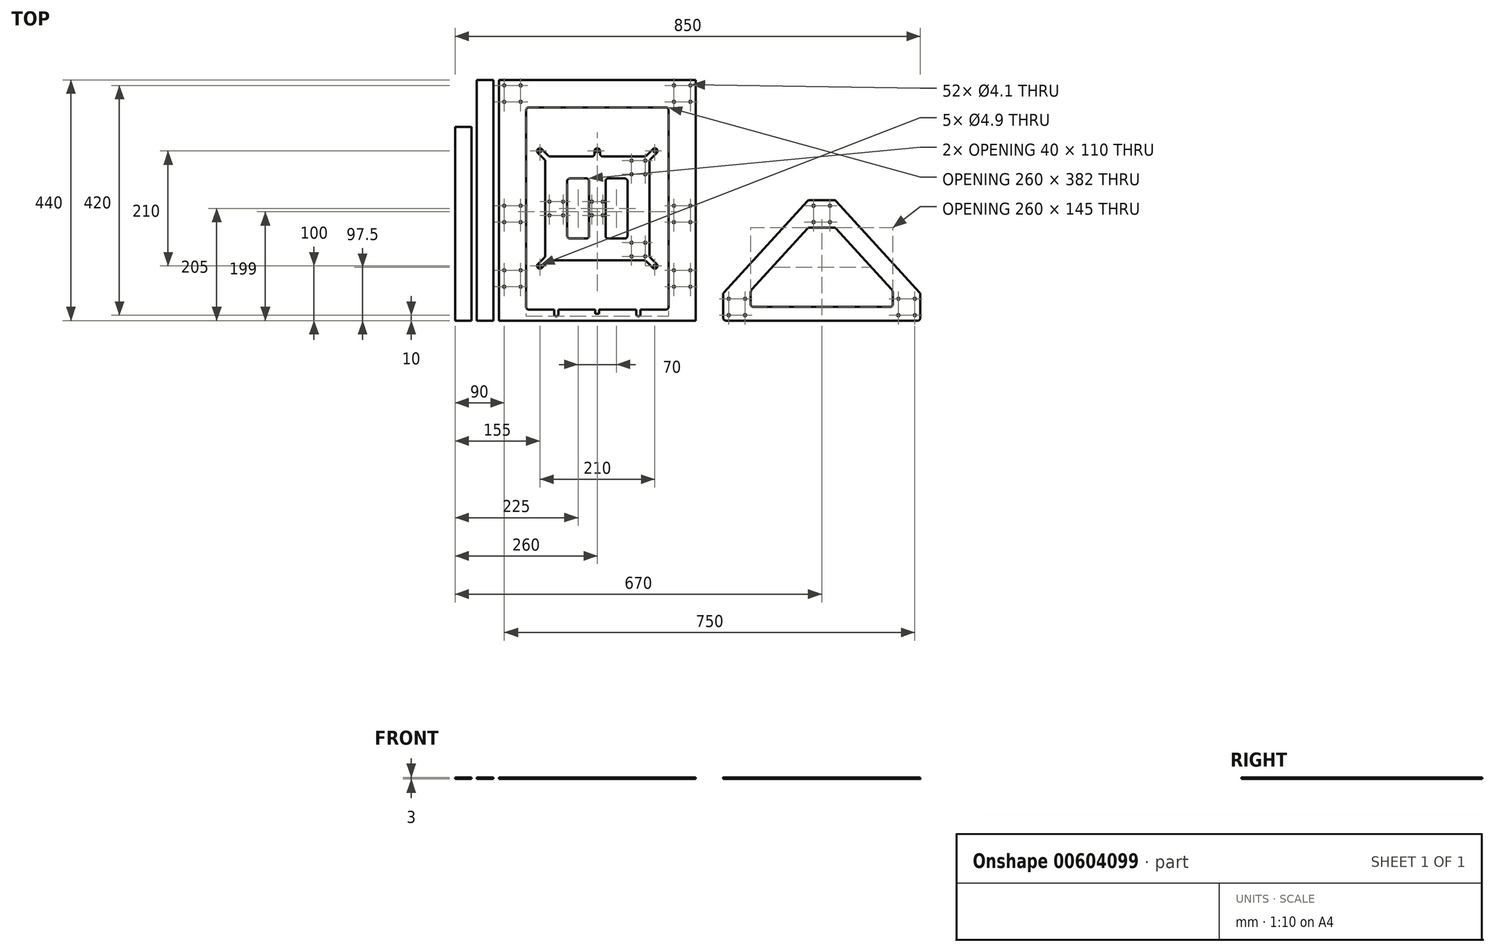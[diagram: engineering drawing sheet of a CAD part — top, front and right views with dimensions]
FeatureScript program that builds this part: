
annotation { "Feature Type Name" : "Feature", "Feature Type Description" : "" }
export const myFeature = defineFeature(function(context is Context, id is Id, definition is map)
    precondition{}
    {
        {
            var Q0;
            Q0=qCreatedBy(makeId("Top.planeOp"),FACE);
            var sketch = newSketch(context, id + "F0", { "sketchPlane" : qUnion([Q0])});
            skLineSegment(sketch, "E0.bottom", {"start": v(0, 0) * mm, "end": v(360, 0) * mm});
            skLineSegment(sketch, "E0.top", {"start": v(0, 440) * mm, "end": v(360, 440) * mm});
            skLineSegment(sketch, "E0.left", {"start": v(0, 0) * mm, "end": v(0, 440) * mm});
            skLineSegment(sketch, "E0.right", {"start": v(360, 0) * mm, "end": v(360, 440) * mm});
            skLineSegment(sketch, "E1.bottom", {"start": v(0, 440) * mm, "end": v(50, 440) * mm, "construction": true});
            skLineSegment(sketch, "E1.top", {"start": v(0, 390) * mm, "end": v(50, 390) * mm, "construction": true});
            skLineSegment(sketch, "E1.left", {"start": v(0, 440) * mm, "end": v(0, 390) * mm, "construction": true});
            skLineSegment(sketch, "E1.right", {"start": v(50, 440) * mm, "end": v(50, 390) * mm, "construction": true});
            skLineSegment(sketch, "E2.bottom", {"start": v(360, 440) * mm, "end": v(310, 440) * mm, "construction": true});
            skLineSegment(sketch, "E2.top", {"start": v(360, 390) * mm, "end": v(310, 390) * mm, "construction": true});
            skLineSegment(sketch, "E2.left", {"start": v(360, 440) * mm, "end": v(360, 390) * mm, "construction": true});
            skLineSegment(sketch, "E2.right", {"start": v(310, 440) * mm, "end": v(310, 390) * mm, "construction": true});
            skLineSegment(sketch, "E3", {"start": v(180, 0) * mm, "end": v(180, 20) * mm, "construction": true});
            skLineSegment(sketch, "E4.bottom", {"start": v(305, 390) * mm, "end": v(55, 390) * mm});
            skLineSegment(sketch, "E4.top", {"start": v(305, 20) * mm, "end": v(259, 20) * mm});
            skLineSegment(sketch, "E4.left", {"start": v(310, 385) * mm, "end": v(310, 25) * mm});
            skLineSegment(sketch, "E4.right", {"start": v(50, 385) * mm, "end": v(50, 25) * mm});
            skLineSegment(sketch, "E5.top", {"start": v(176.5, 12.5) * mm, "end": v(183.5, 12.5) * mm});
            skLineSegment(sketch, "E5.left", {"start": v(176.5, 20) * mm, "end": v(176.5, 12.5) * mm});
            skLineSegment(sketch, "E5.right", {"start": v(183.5, 20) * mm, "end": v(183.5, 12.5) * mm});
            skArc(sketch, "E6", {"start": v(101, 12) * mm, "mid": v(105, 8) * mm, "end": v(109, 12) * mm});
            skLineSegment(sketch, "E7", {"start": v(0, 12) * mm, "end": v(360, 12) * mm, "construction": true});
            skArc(sketch, "E8", {"start": v(251, 12) * mm, "mid": v(255, 8) * mm, "end": v(259, 12) * mm});
            skLineSegment(sketch, "E9.trimOffspring", {"start": v(176.5, 20) * mm, "end": v(109, 20) * mm});
            skCircle(sketch, "E10", {"center": v(10, 62) * mm, "radius": 2.05 * mm});
            skCircle(sketch, "E11.0.1.0", {"center": v(10, 92) * mm, "radius": 2.05 * mm});
            skCircle(sketch, "E11.1.0.0", {"center": v(40, 62) * mm, "radius": 2.05 * mm});
            skCircle(sketch, "E11.1.1.0", {"center": v(40, 92) * mm, "radius": 2.05 * mm});
            skLineSegment(sketch, "E11.direction1", {"start": v(10, 62) * mm, "end": v(40, 62) * mm, "construction": true});
            skLineSegment(sketch, "E11.direction2", {"start": v(10, 62) * mm, "end": v(10, 92) * mm, "construction": true});
            skCircle(sketch, "E12", {"center": v(320, 62) * mm, "radius": 2.05 * mm});
            skCircle(sketch, "E13.0.1.0", {"center": v(320, 92) * mm, "radius": 2.05 * mm});
            skCircle(sketch, "E13.1.0.0", {"center": v(350, 62) * mm, "radius": 2.05 * mm});
            skCircle(sketch, "E13.1.1.0", {"center": v(350, 92) * mm, "radius": 2.05 * mm});
            skLineSegment(sketch, "E13.direction1", {"start": v(320, 62) * mm, "end": v(350, 62) * mm, "construction": true});
            skLineSegment(sketch, "E13.direction2", {"start": v(320, 62) * mm, "end": v(320, 92) * mm, "construction": true});
            skCircle(sketch, "E14", {"center": v(10, 400) * mm, "radius": 2.05 * mm});
            skCircle(sketch, "E15.0.1.0", {"center": v(10, 430) * mm, "radius": 2.05 * mm});
            skCircle(sketch, "E15.1.0.0", {"center": v(40, 400) * mm, "radius": 2.05 * mm});
            skCircle(sketch, "E15.1.1.0", {"center": v(40, 430) * mm, "radius": 2.05 * mm});
            skLineSegment(sketch, "E15.direction1", {"start": v(10, 400) * mm, "end": v(40, 400) * mm, "construction": true});
            skLineSegment(sketch, "E15.direction2", {"start": v(10, 400) * mm, "end": v(10, 430) * mm, "construction": true});
            skCircle(sketch, "E16", {"center": v(320, 400) * mm, "radius": 2.05 * mm});
            skCircle(sketch, "E17.0.1.0", {"center": v(320, 430) * mm, "radius": 2.05 * mm});
            skCircle(sketch, "E17.1.0.0", {"center": v(350, 400) * mm, "radius": 2.05 * mm});
            skCircle(sketch, "E17.1.1.0", {"center": v(350, 430) * mm, "radius": 2.05 * mm});
            skLineSegment(sketch, "E17.direction1", {"start": v(320, 400) * mm, "end": v(350, 400) * mm, "construction": true});
            skLineSegment(sketch, "E17.direction2", {"start": v(320, 400) * mm, "end": v(320, 430) * mm, "construction": true});
            skLineSegment(sketch, "E18", {"start": v(101, 12) * mm, "end": v(101, 20) * mm});
            skLineSegment(sketch, "E19", {"start": v(109, 12) * mm, "end": v(109, 20) * mm});
            skLineSegment(sketch, "E20.trimOffspring", {"start": v(101, 20) * mm, "end": v(55, 20) * mm});
            skLineSegment(sketch, "E21", {"start": v(259, 12) * mm, "end": v(259, 20) * mm});
            skLineSegment(sketch, "E22", {"start": v(251, 12) * mm, "end": v(251, 20) * mm});
            skLineSegment(sketch, "E23.trimOffspring", {"start": v(251, 20) * mm, "end": v(183.5, 20) * mm});
            skLineSegment(sketch, "E24.bottom", {"start": v(350, 92) * mm, "end": v(320, 92) * mm, "construction": true});
            skLineSegment(sketch, "E24.top", {"start": v(350, 62) * mm, "end": v(320, 62) * mm, "construction": true});
            skLineSegment(sketch, "E24.left", {"start": v(350, 92) * mm, "end": v(350, 62) * mm, "construction": true});
            skLineSegment(sketch, "E24.right", {"start": v(320, 92) * mm, "end": v(320, 62) * mm, "construction": true});
            skPoint(sketch, "E24.middle", {"position": v(335, 77) * mm});
            skLineSegment(sketch, "E25", {"start": v(310, 20) * mm, "end": v(360, 20) * mm, "construction": true});
            skLineSegment(sketch, "E26", {"start": v(335, 20) * mm, "end": v(335, 77) * mm, "construction": true});
            skLineSegment(sketch, "E27.bottom", {"start": v(10, 92) * mm, "end": v(40, 92) * mm, "construction": true});
            skLineSegment(sketch, "E27.left", {"start": v(10, 92) * mm, "end": v(10, 62) * mm, "construction": true});
            skLineSegment(sketch, "E27.right", {"start": v(40, 92) * mm, "end": v(40, 62) * mm, "construction": true});
            skPoint(sketch, "E27.middle", {"position": v(25, 77) * mm});
            skLineSegment(sketch, "E28", {"start": v(50, 20) * mm, "end": v(0, 20) * mm, "construction": true});
            skLineSegment(sketch, "E29", {"start": v(25, 20) * mm, "end": v(25, 77) * mm, "construction": true});
            skLineSegment(sketch, "E30.bottom", {"start": v(10, 430) * mm, "end": v(40, 430) * mm, "construction": true});
            skLineSegment(sketch, "E30.left", {"start": v(10, 430) * mm, "end": v(10, 400) * mm, "construction": true});
            skLineSegment(sketch, "E30.right", {"start": v(40, 430) * mm, "end": v(40, 400) * mm, "construction": true});
            skPoint(sketch, "E30.middle", {"position": v(25, 415) * mm});
            skLineSegment(sketch, "E31", {"start": v(25, 390) * mm, "end": v(25, 415) * mm, "construction": true});
            skLineSegment(sketch, "E32", {"start": v(25, 415) * mm, "end": v(50, 415) * mm, "construction": true});
            skLineSegment(sketch, "E33.bottom", {"start": v(350, 430) * mm, "end": v(320, 430) * mm, "construction": true});
            skLineSegment(sketch, "E33.top", {"start": v(350, 400) * mm, "end": v(320, 400) * mm, "construction": true});
            skLineSegment(sketch, "E33.left", {"start": v(350, 430) * mm, "end": v(350, 400) * mm, "construction": true});
            skLineSegment(sketch, "E33.right", {"start": v(320, 430) * mm, "end": v(320, 400) * mm, "construction": true});
            skPoint(sketch, "E33.middle", {"position": v(335, 415) * mm});
            skLineSegment(sketch, "E34", {"start": v(335, 415) * mm, "end": v(335, 390) * mm, "construction": true});
            skLineSegment(sketch, "E35", {"start": v(335, 415) * mm, "end": v(310, 415) * mm, "construction": true});
            skLineSegment(sketch, "E36", {"start": v(0, 220) * mm, "end": v(50, 220) * mm, "construction": true});
            skLineSegment(sketch, "E37", {"start": v(360, 220) * mm, "end": v(310, 220) * mm, "construction": true});
            skLineSegment(sketch, "E38", {"start": v(25, 220) * mm, "end": v(25, 210) * mm, "construction": true});
            skLineSegment(sketch, "E39", {"start": v(335, 220) * mm, "end": v(335, 210) * mm, "construction": true});
            skLineSegment(sketch, "E40.bottom", {"start": v(10, 210) * mm, "end": v(40, 210) * mm, "construction": true});
            skLineSegment(sketch, "E40.top", {"start": v(10, 180) * mm, "end": v(40, 180) * mm, "construction": true});
            skLineSegment(sketch, "E40.left", {"start": v(10, 210) * mm, "end": v(10, 180) * mm, "construction": true});
            skLineSegment(sketch, "E40.right", {"start": v(40, 210) * mm, "end": v(40, 180) * mm, "construction": true});
            skPoint(sketch, "E40.middle", {"position": v(25, 195) * mm});
            skCircle(sketch, "E41", {"center": v(10, 180) * mm, "radius": 2.05 * mm});
            skCircle(sketch, "E42.0.1.0", {"center": v(10, 210) * mm, "radius": 2.05 * mm});
            skCircle(sketch, "E42.1.0.0", {"center": v(40, 180) * mm, "radius": 2.05 * mm});
            skCircle(sketch, "E42.1.1.0", {"center": v(40, 210) * mm, "radius": 2.05 * mm});
            skLineSegment(sketch, "E42.direction2", {"start": v(10, 180) * mm, "end": v(10, 210) * mm, "construction": true});
            skLineSegment(sketch, "E43.bottom", {"start": v(320, 210) * mm, "end": v(350, 210) * mm, "construction": true});
            skLineSegment(sketch, "E43.top", {"start": v(320, 180) * mm, "end": v(350, 180) * mm, "construction": true});
            skLineSegment(sketch, "E43.left", {"start": v(320, 210) * mm, "end": v(320, 180) * mm, "construction": true});
            skLineSegment(sketch, "E43.right", {"start": v(350, 210) * mm, "end": v(350, 180) * mm, "construction": true});
            skPoint(sketch, "E43.middle", {"position": v(335, 195) * mm});
            skCircle(sketch, "E44", {"center": v(320, 180) * mm, "radius": 2.05 * mm});
            skCircle(sketch, "E45.0.1.0", {"center": v(320, 210) * mm, "radius": 2.05 * mm});
            skCircle(sketch, "E45.1.0.0", {"center": v(350, 180) * mm, "radius": 2.05 * mm});
            skCircle(sketch, "E45.1.1.0", {"center": v(350, 210) * mm, "radius": 2.05 * mm});
            skLineSegment(sketch, "E45.direction2", {"start": v(320, 180) * mm, "end": v(320, 210) * mm, "construction": true});
            skPoint(sketch, "E46.visualSharp", {"position": v(0, 0) * mm});
            skPoint(sketch, "E47.visualSharp", {"position": v(50, 20) * mm});
            skArc(sketch, "E47.filletArc", {"start": v(50, 25) * mm, "mid": v(51.46, 21.46) * mm, "end": v(55, 20) * mm});
            skPoint(sketch, "E48.visualSharp", {"position": v(360, 0) * mm});
            skPoint(sketch, "E49.visualSharp", {"position": v(310, 20) * mm});
            skArc(sketch, "E49.filletArc", {"start": v(305, 20) * mm, "mid": v(308.54, 21.46) * mm, "end": v(310, 25) * mm});
            skPoint(sketch, "E50.visualSharp", {"position": v(360, 440) * mm});
            skPoint(sketch, "E51.visualSharp", {"position": v(310, 390) * mm});
            skArc(sketch, "E51.filletArc", {"start": v(310, 385) * mm, "mid": v(308.54, 388.54) * mm, "end": v(305, 390) * mm});
            skPoint(sketch, "E52.visualSharp", {"position": v(50, 390) * mm});
            skArc(sketch, "E52.filletArc", {"start": v(55, 390) * mm, "mid": v(51.46, 388.54) * mm, "end": v(50, 385) * mm});
            skPoint(sketch, "E53.visualSharp", {"position": v(0, 440) * mm});
            skSolve(sketch);
        }
        {
            var Q0;
            Q0=makeQuery(id+"F0.imprint","IMPRINT",FACE,{"disambiguationData":[TD([[makeQuery(id+"F0.imprint","IMPRINT",EDGE,{"derivedFrom":sQuery(id+"F0.wireOp",EDGE,"E0.bottom")}),1.0]])]});
            extrude(context, id + "F1", {"entities" : qUnion([Q0]), "depth" : 3 * mm, "offsetDistance" : 25 * mm});
        }
        {
            var Q0;
            Q0=qCreatedBy(makeId("Top.planeOp"),FACE);
            var sketch = newSketch(context, id + "F2", { "sketchPlane" : qUnion([Q0])});
            skLineSegment(sketch, "E54", {"start": v(310, 205) * mm, "end": v(50, 205) * mm, "construction": true});
            skLineSegment(sketch, "E55", {"start": v(180, 20) * mm, "end": v(180, 390) * mm, "construction": true});
            skLineSegment(sketch, "E56.bottom", {"start": v(255, 280) * mm, "end": v(105, 280) * mm, "construction": true});
            skLineSegment(sketch, "E56.top", {"start": v(255, 130) * mm, "end": v(105, 130) * mm, "construction": true});
            skLineSegment(sketch, "E56.left", {"start": v(255, 280) * mm, "end": v(255, 130) * mm, "construction": true});
            skLineSegment(sketch, "E56.right", {"start": v(105, 280) * mm, "end": v(105, 130) * mm, "construction": true});
            skCircle(sketch, "E57", {"center": v(180, 310) * mm, "radius": 2.45 * mm});
            skLineSegment(sketch, "E58.1", {"start": v(275, 290.86) * mm, "end": v(275, 119.14) * mm});
            skLineSegment(sketch, "E58.2", {"start": v(265.86, 110) * mm, "end": v(180, 110) * mm});
            skLineSegment(sketch, "E58.3", {"start": v(85, 290.86) * mm, "end": v(85, 119.14) * mm});
            skLineSegment(sketch, "E59", {"start": v(75, 310) * mm, "end": v(105, 280) * mm, "construction": true});
            skArc(sketch, "E60.0.startCap", {"start": v(71.46, 306.46) * mm, "mid": v(71.46, 313.54) * mm, "end": v(78.54, 313.54) * mm});
            skLineSegment(sketch, "E60.0.left", {"start": v(78.54, 313.54) * mm, "end": v(90.6, 301.46) * mm});
            skLineSegment(sketch, "E60.0.right", {"start": v(71.46, 306.46) * mm, "end": v(83.54, 294.4) * mm});
            skPoint(sketch, "E61", {"position": v(282.5, 205) * mm});
            skCircle(sketch, "E62", {"center": v(75, 310) * mm, "radius": 2.45 * mm});
            skArc(sketch, "E63.1.0", {"start": v(78.54, 96.46) * mm, "mid": v(71.46, 96.46) * mm, "end": v(71.46, 103.54) * mm});
            skCircle(sketch, "E63.1.1", {"center": v(75, 100) * mm, "radius": 2.45 * mm});
            skLineSegment(sketch, "E63.1.2", {"start": v(78.54, 96.46) * mm, "end": v(90.6, 108.54) * mm});
            skLineSegment(sketch, "E63.1.3", {"start": v(71.46, 103.54) * mm, "end": v(83.54, 115.6) * mm});
            skLineSegment(sketch, "E63.1.4", {"start": v(75, 100) * mm, "end": v(105, 130) * mm, "construction": true});
            skArc(sketch, "E63.2.0", {"start": v(288.54, 103.54) * mm, "mid": v(288.54, 96.46) * mm, "end": v(281.46, 96.46) * mm});
            skCircle(sketch, "E63.2.1", {"center": v(285, 100) * mm, "radius": 2.45 * mm});
            skLineSegment(sketch, "E63.2.2", {"start": v(288.54, 103.54) * mm, "end": v(276.46, 115.6) * mm});
            skLineSegment(sketch, "E63.2.3", {"start": v(281.46, 96.46) * mm, "end": v(269.4, 108.54) * mm});
            skLineSegment(sketch, "E63.2.4", {"start": v(285, 100) * mm, "end": v(255, 130) * mm, "construction": true});
            skArc(sketch, "E63.3.0", {"start": v(281.46, 313.54) * mm, "mid": v(288.54, 313.54) * mm, "end": v(288.54, 306.46) * mm});
            skCircle(sketch, "E63.3.1", {"center": v(285, 310) * mm, "radius": 2.45 * mm});
            skLineSegment(sketch, "E63.3.2", {"start": v(281.46, 313.54) * mm, "end": v(269.4, 301.46) * mm});
            skLineSegment(sketch, "E63.3.3", {"start": v(288.54, 306.46) * mm, "end": v(276.46, 294.4) * mm});
            skLineSegment(sketch, "E63.3.4", {"start": v(285, 310) * mm, "end": v(255, 280) * mm, "construction": true});
            skLineSegment(sketch, "E64", {"start": v(180, 310) * mm, "end": v(180, 280) * mm, "construction": true});
            skArc(sketch, "E65.0.startCap", {"start": v(175, 310) * mm, "mid": v(180, 315) * mm, "end": v(185, 310) * mm});
            skLineSegment(sketch, "E65.0.left", {"start": v(185, 310) * mm, "end": v(185, 305) * mm});
            skLineSegment(sketch, "E65.0.right", {"start": v(175, 310) * mm, "end": v(175, 305) * mm});
            skLineSegment(sketch, "E66.trimOffspring", {"start": v(170, 300) * mm, "end": v(94.14, 300) * mm});
            skLineSegment(sketch, "E67", {"start": v(265.86, 300) * mm, "end": v(190, 300) * mm});
            skLineSegment(sketch, "E68", {"start": v(94.14, 110) * mm, "end": v(180, 110) * mm});
            skLineSegment(sketch, "E69", {"start": v(75, 310) * mm, "end": v(180, 310) * mm, "construction": true});
            skLineSegment(sketch, "E70.bottom", {"start": v(92.5, 217.5) * mm, "end": v(117.5, 217.5) * mm, "construction": true});
            skLineSegment(sketch, "E70.top", {"start": v(92.5, 192.5) * mm, "end": v(117.5, 192.5) * mm, "construction": true});
            skLineSegment(sketch, "E70.left", {"start": v(92.5, 217.5) * mm, "end": v(92.5, 192.5) * mm, "construction": true});
            skLineSegment(sketch, "E70.right", {"start": v(117.5, 217.5) * mm, "end": v(117.5, 192.5) * mm, "construction": true});
            skPoint(sketch, "E70.middle", {"position": v(105, 205) * mm});
            skCircle(sketch, "E71", {"center": v(92.5, 217.5) * mm, "radius": 2.05 * mm});
            skCircle(sketch, "E72", {"center": v(117.5, 217.5) * mm, "radius": 2.05 * mm});
            skCircle(sketch, "E73", {"center": v(117.5, 192.5) * mm, "radius": 2.05 * mm});
            skCircle(sketch, "E74", {"center": v(92.5, 192.5) * mm, "radius": 2.05 * mm});
            skLineSegment(sketch, "E75.bottom", {"start": v(242.5, 292.5) * mm, "end": v(267.5, 292.5) * mm, "construction": true});
            skLineSegment(sketch, "E75.top", {"start": v(242.5, 267.5) * mm, "end": v(267.5, 267.5) * mm, "construction": true});
            skLineSegment(sketch, "E75.left", {"start": v(242.5, 292.5) * mm, "end": v(242.5, 267.5) * mm, "construction": true});
            skLineSegment(sketch, "E75.right", {"start": v(267.5, 292.5) * mm, "end": v(267.5, 267.5) * mm, "construction": true});
            skPoint(sketch, "E75.middle", {"position": v(255, 280) * mm});
            skCircle(sketch, "E76", {"center": v(242.5, 292.5) * mm, "radius": 2.05 * mm});
            skCircle(sketch, "E77", {"center": v(267.5, 292.5) * mm, "radius": 2.05 * mm});
            skCircle(sketch, "E78", {"center": v(267.5, 267.5) * mm, "radius": 2.05 * mm});
            skCircle(sketch, "E79", {"center": v(242.5, 267.5) * mm, "radius": 2.05 * mm});
            skLineSegment(sketch, "E80.bottom", {"start": v(242.5, 142.5) * mm, "end": v(267.5, 142.5) * mm, "construction": true});
            skLineSegment(sketch, "E80.top", {"start": v(242.5, 117.5) * mm, "end": v(267.5, 117.5) * mm, "construction": true});
            skLineSegment(sketch, "E80.left", {"start": v(242.5, 142.5) * mm, "end": v(242.5, 117.5) * mm, "construction": true});
            skLineSegment(sketch, "E80.right", {"start": v(267.5, 142.5) * mm, "end": v(267.5, 117.5) * mm, "construction": true});
            skPoint(sketch, "E80.middle", {"position": v(255, 130) * mm});
            skCircle(sketch, "E81", {"center": v(242.5, 142.5) * mm, "radius": 2.05 * mm});
            skCircle(sketch, "E82", {"center": v(267.5, 142.5) * mm, "radius": 2.05 * mm});
            skCircle(sketch, "E83", {"center": v(267.5, 117.5) * mm, "radius": 2.05 * mm});
            skCircle(sketch, "E84", {"center": v(242.5, 117.5) * mm, "radius": 2.05 * mm});
            skLineSegment(sketch, "E85.bottom", {"start": v(130, 260) * mm, "end": v(160, 260) * mm});
            skLineSegment(sketch, "E85.top", {"start": v(130, 150) * mm, "end": v(160, 150) * mm});
            skLineSegment(sketch, "E85.left", {"start": v(125, 255) * mm, "end": v(125, 155) * mm});
            skLineSegment(sketch, "E85.right", {"start": v(165, 255) * mm, "end": v(165, 155) * mm});
            skPoint(sketch, "E85.middle", {"position": v(145, 205) * mm});
            skLineSegment(sketch, "E86.bottom", {"start": v(200, 260) * mm, "end": v(230, 260) * mm});
            skLineSegment(sketch, "E86.top", {"start": v(200, 150) * mm, "end": v(230, 150) * mm});
            skLineSegment(sketch, "E86.left", {"start": v(195, 255) * mm, "end": v(195, 155) * mm});
            skLineSegment(sketch, "E86.right", {"start": v(235, 255) * mm, "end": v(235, 155) * mm});
            skPoint(sketch, "E86.middle", {"position": v(215, 205) * mm});
            skLineSegment(sketch, "E87", {"start": v(195, 150) * mm, "end": v(165, 150) * mm, "construction": true});
            skLineSegment(sketch, "E88", {"start": v(195, 260) * mm, "end": v(165, 260) * mm, "construction": true});
            skLineSegment(sketch, "E89", {"start": v(180, 260) * mm, "end": v(180, 150) * mm, "construction": true});
            skLineSegment(sketch, "E90.bottom", {"start": v(75, 310) * mm, "end": v(285, 310) * mm, "construction": true});
            skLineSegment(sketch, "E90.top", {"start": v(75, 100) * mm, "end": v(285, 100) * mm, "construction": true});
            skLineSegment(sketch, "E90.left", {"start": v(75, 310) * mm, "end": v(75, 100) * mm, "construction": true});
            skLineSegment(sketch, "E90.right", {"start": v(285, 310) * mm, "end": v(285, 100) * mm, "construction": true});
            skPoint(sketch, "E90.middle", {"position": v(180, 205) * mm});
            skLineSegment(sketch, "E91.bottom", {"start": v(170, 217.5) * mm, "end": v(190, 217.5) * mm, "construction": true});
            skLineSegment(sketch, "E91.top", {"start": v(170, 192.5) * mm, "end": v(190, 192.5) * mm, "construction": true});
            skLineSegment(sketch, "E91.left", {"start": v(170, 217.5) * mm, "end": v(170, 192.5) * mm, "construction": true});
            skLineSegment(sketch, "E91.right", {"start": v(190, 217.5) * mm, "end": v(190, 192.5) * mm, "construction": true});
            skCircle(sketch, "E92", {"center": v(170, 217.5) * mm, "radius": 2.05 * mm});
            skCircle(sketch, "E93", {"center": v(190, 217.5) * mm, "radius": 2.05 * mm});
            skCircle(sketch, "E94", {"center": v(190, 192.5) * mm, "radius": 2.05 * mm});
            skCircle(sketch, "E95", {"center": v(170, 192.5) * mm, "radius": 2.05 * mm});
            skPoint(sketch, "E96.visualSharp", {"position": v(125, 260) * mm});
            skArc(sketch, "E96.filletArc", {"start": v(130, 260) * mm, "mid": v(126.46, 258.54) * mm, "end": v(125, 255) * mm});
            skPoint(sketch, "E97.visualSharp", {"position": v(165, 150) * mm});
            skArc(sketch, "E97.filletArc", {"start": v(160, 150) * mm, "mid": v(163.54, 151.46) * mm, "end": v(165, 155) * mm});
            skPoint(sketch, "E98.visualSharp", {"position": v(125, 150) * mm});
            skArc(sketch, "E98.filletArc", {"start": v(125, 155) * mm, "mid": v(126.46, 151.46) * mm, "end": v(130, 150) * mm});
            skPoint(sketch, "E99.visualSharp", {"position": v(195, 260) * mm});
            skArc(sketch, "E99.filletArc", {"start": v(200, 260) * mm, "mid": v(196.46, 258.54) * mm, "end": v(195, 255) * mm});
            skPoint(sketch, "E100.visualSharp", {"position": v(165, 260) * mm});
            skArc(sketch, "E100.filletArc", {"start": v(165, 255) * mm, "mid": v(163.54, 258.54) * mm, "end": v(160, 260) * mm});
            skPoint(sketch, "E101.visualSharp", {"position": v(195, 150) * mm});
            skArc(sketch, "E101.filletArc", {"start": v(195, 155) * mm, "mid": v(196.46, 151.46) * mm, "end": v(200, 150) * mm});
            skPoint(sketch, "E102.visualSharp", {"position": v(235, 150) * mm});
            skArc(sketch, "E102.filletArc", {"start": v(230, 150) * mm, "mid": v(233.54, 151.46) * mm, "end": v(235, 155) * mm});
            skPoint(sketch, "E103.visualSharp", {"position": v(235, 260) * mm});
            skArc(sketch, "E103.filletArc", {"start": v(235, 255) * mm, "mid": v(233.54, 258.54) * mm, "end": v(230, 260) * mm});
            skPoint(sketch, "E104.visualSharp", {"position": v(175, 300) * mm});
            skArc(sketch, "E104.filletArc", {"start": v(170, 300) * mm, "mid": v(173.54, 301.46) * mm, "end": v(175, 305) * mm});
            skPoint(sketch, "E105.visualSharp", {"position": v(275, 117.07) * mm});
            skArc(sketch, "E105.filletArc", {"start": v(275, 119.14) * mm, "mid": v(275.38, 117.23) * mm, "end": v(276.46, 115.6) * mm});
            skPoint(sketch, "E106.visualSharp", {"position": v(92.07, 110) * mm});
            skArc(sketch, "E106.filletArc", {"start": v(94.14, 110) * mm, "mid": v(92.23, 109.62) * mm, "end": v(90.6, 108.54) * mm});
            skPoint(sketch, "E107.visualSharp", {"position": v(267.93, 110) * mm});
            skArc(sketch, "E107.filletArc", {"start": v(269.4, 108.54) * mm, "mid": v(267.77, 109.62) * mm, "end": v(265.86, 110) * mm});
            skPoint(sketch, "E108.visualSharp", {"position": v(85, 117.07) * mm});
            skArc(sketch, "E108.filletArc", {"start": v(83.54, 115.6) * mm, "mid": v(84.62, 117.23) * mm, "end": v(85, 119.14) * mm});
            skPoint(sketch, "E109.visualSharp", {"position": v(85, 292.93) * mm});
            skArc(sketch, "E109.filletArc", {"start": v(85, 290.86) * mm, "mid": v(84.62, 292.77) * mm, "end": v(83.54, 294.4) * mm});
            skPoint(sketch, "E110.visualSharp", {"position": v(185, 300) * mm});
            skArc(sketch, "E110.filletArc", {"start": v(185, 305) * mm, "mid": v(186.46, 301.46) * mm, "end": v(190, 300) * mm});
            skPoint(sketch, "E111.visualSharp", {"position": v(275, 292.93) * mm});
            skArc(sketch, "E111.filletArc", {"start": v(276.46, 294.4) * mm, "mid": v(275.38, 292.77) * mm, "end": v(275, 290.86) * mm});
            skPoint(sketch, "E112.visualSharp", {"position": v(267.93, 300) * mm});
            skArc(sketch, "E112.filletArc", {"start": v(265.86, 300) * mm, "mid": v(267.77, 300.38) * mm, "end": v(269.4, 301.46) * mm});
            skPoint(sketch, "E113.visualSharp", {"position": v(92.07, 300) * mm});
            skArc(sketch, "E113.filletArc", {"start": v(90.6, 301.46) * mm, "mid": v(92.23, 300.38) * mm, "end": v(94.14, 300) * mm});
            skSolve(sketch);
        }
        {
            var Q0;
            Q0 = qSketchRegion(id + "F2", true);
            extrude(context, id + "F3", {"entities" : qUnion([Q0]), "operationType" : NewBodyOperationType.ADD, "depth" : 3 * mm, "offsetDistance" : 25 * mm});
        }
        {
            var Q0;
            Q0=qCreatedBy(makeId("Top.planeOp"),FACE);
            var sketch = newSketch(context, id + "F4", { "sketchPlane" : qUnion([Q0])});
            skLineSegment(sketch, "E114", {"start": v(415, 0) * mm, "end": v(765, 0) * mm});
            skLineSegment(sketch, "E115", {"start": v(590, 0) * mm, "end": v(590, 220) * mm, "construction": true});
            skLineSegment(sketch, "E116", {"start": v(616.49, 218.37) * mm, "end": v(768.7, 51.43) * mm});
            skLineSegment(sketch, "E117", {"start": v(563.51, 218.37) * mm, "end": v(411.3, 51.43) * mm});
            skLineSegment(sketch, "E118", {"start": v(567.2, 220) * mm, "end": v(612.8, 220) * mm});
            skLineSegment(sketch, "E119.bottom", {"start": v(575, 210) * mm, "end": v(605, 210) * mm, "construction": true});
            skLineSegment(sketch, "E119.top", {"start": v(575, 180) * mm, "end": v(605, 180) * mm, "construction": true});
            skLineSegment(sketch, "E119.left", {"start": v(575, 210) * mm, "end": v(575, 180) * mm, "construction": true});
            skLineSegment(sketch, "E119.right", {"start": v(605, 210) * mm, "end": v(605, 180) * mm, "construction": true});
            skPoint(sketch, "E119.middle", {"position": v(590, 195) * mm});
            skCircle(sketch, "E120", {"center": v(575, 210) * mm, "radius": 2.05 * mm});
            skCircle(sketch, "E121", {"center": v(605, 210) * mm, "radius": 2.05 * mm});
            skCircle(sketch, "E122", {"center": v(605, 180) * mm, "radius": 2.05 * mm});
            skCircle(sketch, "E123", {"center": v(575, 180) * mm, "radius": 2.05 * mm});
            skLineSegment(sketch, "E124", {"start": v(410, 48.06) * mm, "end": v(410, 5) * mm});
            skLineSegment(sketch, "E125", {"start": v(770, 48.06) * mm, "end": v(770, 5) * mm});
            skLineSegment(sketch, "E126", {"start": v(410, 25) * mm, "end": v(770, 25) * mm, "construction": true});
            skLineSegment(sketch, "E127.bottom", {"start": v(420, 40) * mm, "end": v(450, 40) * mm, "construction": true});
            skLineSegment(sketch, "E127.top", {"start": v(420, 10) * mm, "end": v(450, 10) * mm, "construction": true});
            skLineSegment(sketch, "E127.left", {"start": v(420, 40) * mm, "end": v(420, 10) * mm, "construction": true});
            skLineSegment(sketch, "E127.right", {"start": v(450, 40) * mm, "end": v(450, 10) * mm, "construction": true});
            skPoint(sketch, "E127.middle", {"position": v(435, 25) * mm});
            skCircle(sketch, "E128", {"center": v(420, 40) * mm, "radius": 2.05 * mm});
            skCircle(sketch, "E129", {"center": v(450, 40) * mm, "radius": 2.05 * mm});
            skCircle(sketch, "E130", {"center": v(450, 10) * mm, "radius": 2.05 * mm});
            skCircle(sketch, "E131", {"center": v(420, 10) * mm, "radius": 2.05 * mm});
            skLineSegment(sketch, "E132.bottom", {"start": v(730, 40) * mm, "end": v(760, 40) * mm, "construction": true});
            skLineSegment(sketch, "E132.top", {"start": v(730, 10) * mm, "end": v(760, 10) * mm, "construction": true});
            skLineSegment(sketch, "E132.left", {"start": v(730, 40) * mm, "end": v(730, 10) * mm, "construction": true});
            skLineSegment(sketch, "E132.right", {"start": v(760, 40) * mm, "end": v(760, 10) * mm, "construction": true});
            skPoint(sketch, "E132.middle", {"position": v(745, 25) * mm});
            skCircle(sketch, "E133", {"center": v(730, 40) * mm, "radius": 2.05 * mm});
            skCircle(sketch, "E134", {"center": v(760, 40) * mm, "radius": 2.05 * mm});
            skCircle(sketch, "E135", {"center": v(760, 10) * mm, "radius": 2.05 * mm});
            skCircle(sketch, "E136", {"center": v(730, 10) * mm, "radius": 2.05 * mm});
            skLineSegment(sketch, "E137.bottom", {"start": v(410, 50) * mm, "end": v(460, 50) * mm, "construction": true});
            skLineSegment(sketch, "E137.top", {"start": v(410, 0) * mm, "end": v(460, 0) * mm, "construction": true});
            skLineSegment(sketch, "E137.left", {"start": v(410, 50) * mm, "end": v(410, 0) * mm, "construction": true});
            skLineSegment(sketch, "E137.right", {"start": v(460, 50) * mm, "end": v(460, 0) * mm, "construction": true});
            skLineSegment(sketch, "E138.bottom", {"start": v(770, 50) * mm, "end": v(720, 50) * mm, "construction": true});
            skLineSegment(sketch, "E138.top", {"start": v(770, 0) * mm, "end": v(720, 0) * mm, "construction": true});
            skLineSegment(sketch, "E138.left", {"start": v(770, 50) * mm, "end": v(770, 0) * mm, "construction": true});
            skLineSegment(sketch, "E138.right", {"start": v(720, 50) * mm, "end": v(720, 0) * mm, "construction": true});
            skLineSegment(sketch, "E139.bottom", {"start": v(615, 220) * mm, "end": v(565, 220) * mm, "construction": true});
            skLineSegment(sketch, "E139.top", {"start": v(612.8, 170) * mm, "end": v(567.2, 170) * mm});
            skLineSegment(sketch, "E139.left", {"start": v(615, 220) * mm, "end": v(615, 170) * mm, "construction": true});
            skLineSegment(sketch, "E139.right", {"start": v(565, 220) * mm, "end": v(565, 170) * mm, "construction": true});
            skLineSegment(sketch, "E140", {"start": v(465, 25) * mm, "end": v(715, 25) * mm});
            skLineSegment(sketch, "E141", {"start": v(616.49, 168.37) * mm, "end": v(716.74, 58.41) * mm});
            skLineSegment(sketch, "E142", {"start": v(563.51, 168.37) * mm, "end": v(463.26, 58.41) * mm});
            skLineSegment(sketch, "E143", {"start": v(460, 30) * mm, "end": v(460, 50) * mm});
            skLineSegment(sketch, "E144", {"start": v(720, 50) * mm, "end": v(720, 30) * mm});
            skArc(sketch, "E145", {"start": v(463.26, 58.41) * mm, "mid": v(460.84, 54.51) * mm, "end": v(460, 50) * mm});
            skLineSegment(sketch, "E146", {"start": v(460, 50) * mm, "end": v(472.49, 50) * mm, "construction": true});
            skLineSegment(sketch, "E147", {"start": v(463.26, 58.41) * mm, "end": v(472.49, 50) * mm, "construction": true});
            skArc(sketch, "E148", {"start": v(720, 50) * mm, "mid": v(719.16, 54.51) * mm, "end": v(716.74, 58.41) * mm});
            skLineSegment(sketch, "E149", {"start": v(720, 50) * mm, "end": v(707.51, 50) * mm, "construction": true});
            skLineSegment(sketch, "E150", {"start": v(707.51, 50) * mm, "end": v(716.74, 58.41) * mm, "construction": true});
            skPoint(sketch, "E151.visualSharp", {"position": v(565, 170) * mm});
            skArc(sketch, "E151.filletArc", {"start": v(567.2, 170) * mm, "mid": v(565.19, 169.57) * mm, "end": v(563.51, 168.37) * mm});
            skPoint(sketch, "E152.visualSharp", {"position": v(615, 170) * mm});
            skArc(sketch, "E152.filletArc", {"start": v(616.49, 168.37) * mm, "mid": v(614.81, 169.57) * mm, "end": v(612.8, 170) * mm});
            skPoint(sketch, "E153.visualSharp", {"position": v(720, 25) * mm});
            skArc(sketch, "E153.filletArc", {"start": v(715, 25) * mm, "mid": v(718.54, 26.46) * mm, "end": v(720, 30) * mm});
            skPoint(sketch, "E154.visualSharp", {"position": v(460, 25) * mm});
            skArc(sketch, "E154.filletArc", {"start": v(460, 30) * mm, "mid": v(461.46, 26.46) * mm, "end": v(465, 25) * mm});
            skPoint(sketch, "E155.visualSharp", {"position": v(565, 220) * mm});
            skArc(sketch, "E155.filletArc", {"start": v(567.2, 220) * mm, "mid": v(565.19, 219.57) * mm, "end": v(563.51, 218.37) * mm});
            skPoint(sketch, "E156.visualSharp", {"position": v(615, 220) * mm});
            skArc(sketch, "E156.filletArc", {"start": v(616.49, 218.37) * mm, "mid": v(614.81, 219.57) * mm, "end": v(612.8, 220) * mm});
            skPoint(sketch, "E157.visualSharp", {"position": v(770, 50) * mm});
            skArc(sketch, "E157.filletArc", {"start": v(770, 48.06) * mm, "mid": v(769.66, 49.87) * mm, "end": v(768.7, 51.43) * mm});
            skPoint(sketch, "E158.visualSharp", {"position": v(410, 50) * mm});
            skArc(sketch, "E158.filletArc", {"start": v(411.3, 51.43) * mm, "mid": v(410.34, 49.87) * mm, "end": v(410, 48.06) * mm});
            skPoint(sketch, "E159.visualSharp", {"position": v(410, 0) * mm});
            skArc(sketch, "E159.filletArc", {"start": v(410, 5) * mm, "mid": v(411.46, 1.46) * mm, "end": v(415, 0) * mm});
            skPoint(sketch, "E160.visualSharp", {"position": v(770, 0) * mm});
            skArc(sketch, "E160.filletArc", {"start": v(765, 0) * mm, "mid": v(768.54, 1.46) * mm, "end": v(770, 5) * mm});
            skSolve(sketch);
        }
        {
            var Q0;
            Q0 = qSketchRegion(id + "F4", true);
            extrude(context, id + "F5", {"entities" : qUnion([Q0]), "depth" : 3 * mm, "offsetDistance" : 25 * mm});
        }
        {
            var Q0;
            Q0=qCreatedBy(makeId("Top.planeOp"),FACE);
            var sketch = newSketch(context, id + "F6", { "sketchPlane" : qUnion([Q0])});
            skLineSegment(sketch, "E161.bottom", {"start": v(-10, 0) * mm, "end": v(-40, 0) * mm});
            skLineSegment(sketch, "E161.top", {"start": v(-10, 440) * mm, "end": v(-40, 440) * mm});
            skLineSegment(sketch, "E161.left", {"start": v(-10, 0) * mm, "end": v(-10, 440) * mm});
            skLineSegment(sketch, "E161.right", {"start": v(-40, 0) * mm, "end": v(-40, 440) * mm});
            skSolve(sketch);
        }
        {
            var Q0;
            Q0=qCreatedBy(makeId("Top.planeOp"),FACE);
            var sketch = newSketch(context, id + "F7", { "sketchPlane" : qUnion([Q0])});
            skLineSegment(sketch, "E162.bottom", {"start": v(-50, 0) * mm, "end": v(-80, 0) * mm});
            skLineSegment(sketch, "E162.top", {"start": v(-50, 354) * mm, "end": v(-80, 354) * mm});
            skLineSegment(sketch, "E162.left", {"start": v(-50, 0) * mm, "end": v(-50, 354) * mm});
            skLineSegment(sketch, "E162.right", {"start": v(-80, 0) * mm, "end": v(-80, 354) * mm});
            skSolve(sketch);
        }
        {
            var Q0;
            Q0 = qSketchRegion(id + "F6", true);
            var Q1;
            Q1 = qSketchRegion(id + "F7", true);
            extrude(context, id + "F8", {"entities" : qUnion([Q0, Q1]), "depth" : 3 * mm, "offsetDistance" : 25 * mm});
        }
    });
